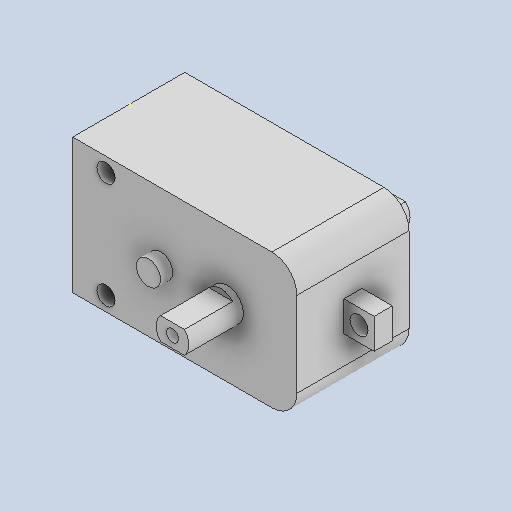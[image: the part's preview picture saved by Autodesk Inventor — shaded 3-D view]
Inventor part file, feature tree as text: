
AUTODESK INVENTOR PART (.ipt)
format: ipt  version: 2022 (Build 260153070, 153G)  size: 169,472 bytes
history: native  units: in
note: dims shown in document units (in); Inventor stores cm internally (conversion verified against a paired STEP export)
features: sketch x6, other x5, plane x2
ambient origin geometry x8: Origin, YZ Plane, XZ Plane, XY Plane, X Axis, Y Axis, Z Axis, Center Point
bodies: Solid1 (feature_tree)
feature tree (13):
  other  "TT motor output.ipt"
  other  "Solid1::TT motor output.ipt"
  other  "TaggingFeature1"
  sketch  "Sketch1"  dims[d0=0.3937in]
  sketch  "Sketch2"
  sketch  "Sketch3"
  sketch  "Sketch4"
  sketch  "Sketch5"
  sketch  "Sketch6"
  plane  "Work Plane1"
  plane  "Work Plane2"
  other  "Work Axis1"
  other  "Work Point1"
